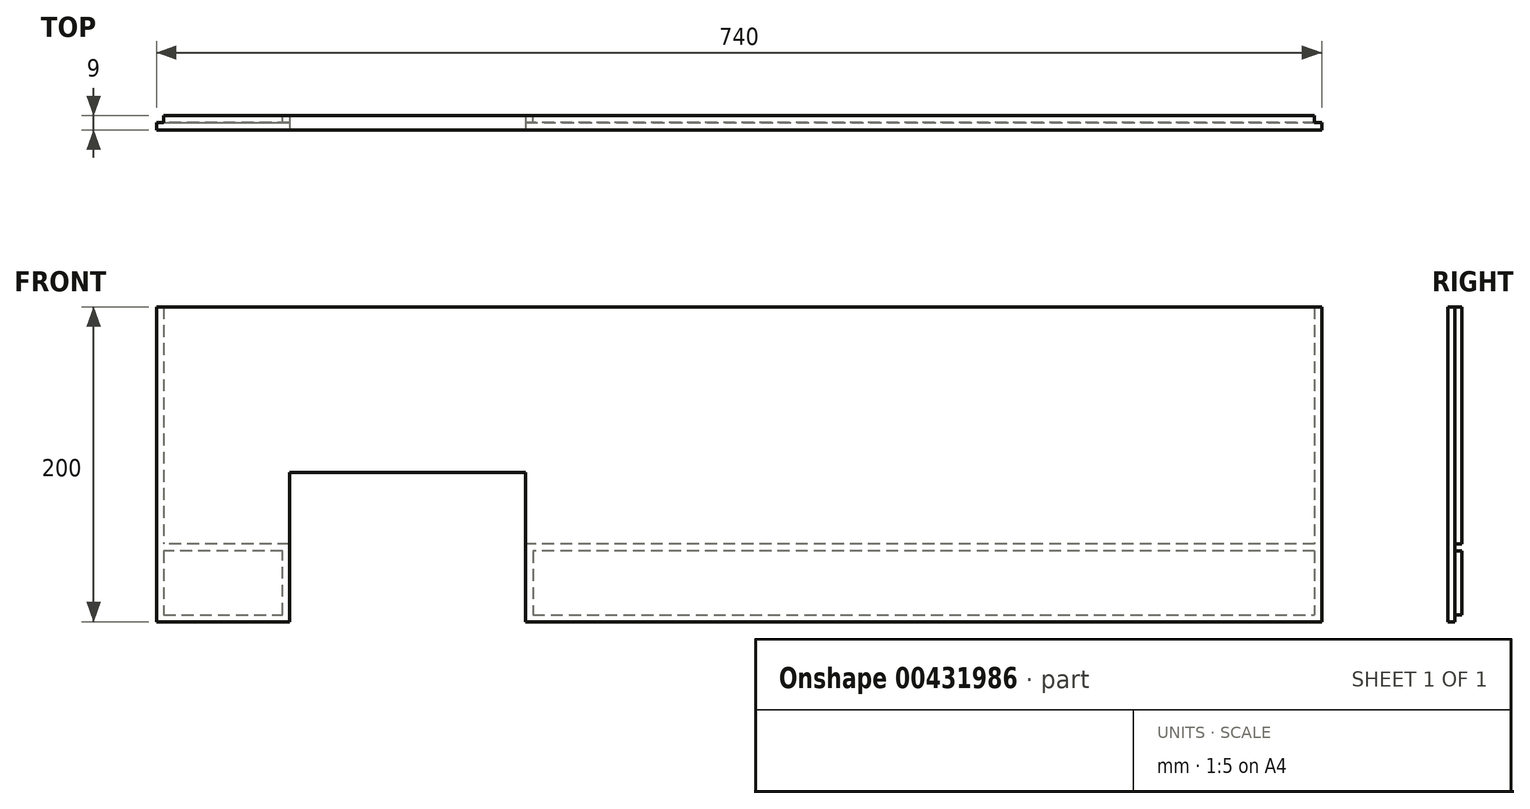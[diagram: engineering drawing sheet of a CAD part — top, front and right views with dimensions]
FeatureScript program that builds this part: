
annotation { "Feature Type Name" : "Feature", "Feature Type Description" : "" }
export const myFeature = defineFeature(function(context is Context, id is Id, definition is map)
    precondition{}
    {
        {
            var Q0;
            Q0=qCreatedBy(makeId("Front.planeOp"),FACE);
            var sketch = newSketch(context, id + "F0", { "sketchPlane" : qUnion([Q0])});
            skLineSegment(sketch, "E0.bottom", {"start": v(-370, 100) * mm, "end": v(370, 100) * mm});
            skLineSegment(sketch, "E0.top", {"start": v(-370, -100) * mm, "end": v(370, -100) * mm});
            skLineSegment(sketch, "E0.left", {"start": v(-370, 100) * mm, "end": v(-370, -100) * mm});
            skLineSegment(sketch, "E0.right", {"start": v(370, 100) * mm, "end": v(370, -100) * mm});
            skPoint(sketch, "E0.middle", {"position": v(0, 0) * mm});
            skSolve(sketch);
        }
        {
            var Q0;
            Q0=makeQuery(id+"F0.imprint","IMPRINT",FACE,{"disambiguationData":[TD([[makeQuery(id+"F0.imprint","IMPRINT",EDGE,{"derivedFrom":sQuery(id+"F0.wireOp",EDGE,"E0.bottom")}),-1.0]])]});
            extrude(context, id + "F1", {"entities" : qUnion([Q0]), "depth" : 9 * mm, "offsetDistance" : 25 * mm});
        }
        {
            var Q0;
            Q0=makeQuery(id+"F1.opExtrude","SWEPT_FACE",FACE,{"disambiguationData":[OSD([sQuery(id+"F0.wireOp",EDGE,"E0.right")])]});
            var sketch = newSketch(context, id + "F2", { "sketchPlane" : qUnion([Q0])});
            skLineSegment(sketch, "E1.bottom", {"start": v(0, 100) * mm, "end": v(-4.5, 100) * mm});
            skLineSegment(sketch, "E1.top", {"start": v(0, -100) * mm, "end": v(-4.5, -100) * mm});
            skLineSegment(sketch, "E1.left", {"start": v(0, 100) * mm, "end": v(0, -100) * mm});
            skLineSegment(sketch, "E1.right", {"start": v(-4.5, 100) * mm, "end": v(-4.5, -100) * mm});
            skSolve(sketch);
        }
        {
            var Q0;
            Q0=qSketchRegion(id+"F2",true);
            extrude(context, id + "F3", {"entities" : qUnion([Q0]), "operationType" : NewBodyOperationType.REMOVE, "oppositeDirection" : true, "depth" : 4.5 * mm, "offsetDistance" : 25 * mm});
        }
        {
            var Q0;
            Q0=makeQuery(id+"F1.opExtrude","SWEPT_FACE",FACE,{"disambiguationData":[OSD([sQuery(id+"F0.wireOp",EDGE,"E0.left")])]});
            var sketch = newSketch(context, id + "F4", { "sketchPlane" : qUnion([Q0])});
            skLineSegment(sketch, "E2.bottom", {"start": v(0, 100) * mm, "end": v(4.5, 100) * mm});
            skLineSegment(sketch, "E2.top", {"start": v(0, -100) * mm, "end": v(4.5, -100) * mm});
            skLineSegment(sketch, "E2.left", {"start": v(0, 100) * mm, "end": v(0, -100) * mm});
            skLineSegment(sketch, "E2.right", {"start": v(4.5, 100) * mm, "end": v(4.5, -100) * mm});
            skSolve(sketch);
        }
        {
            var Q0;
            Q0=qSketchRegion(id+"F4",true);
            extrude(context, id + "F5", {"entities" : qUnion([Q0]), "operationType" : NewBodyOperationType.REMOVE, "oppositeDirection" : true, "depth" : 4.5 * mm, "offsetDistance" : 25 * mm});
        }
        {
            var Q0;
            Q0=makeQuery(id+"F1.opExtrude","CAP_FACE",FACE,{"disambiguationData":[OSD([sQuery(id+"F0.wireOp",EDGE,"E0.bottom"),sQuery(id+"F0.wireOp",EDGE,"E0.top"),sQuery(id+"F0.wireOp",EDGE,"E0.left"),sQuery(id+"F0.wireOp",EDGE,"E0.right")])],"isStart":true});
            var sketch = newSketch(context, id + "F6", { "sketchPlane" : qUnion([Q0])});
            skLineSegment(sketch, "E3.bottom", {"start": v(-365.5, -50.5) * mm, "end": v(365.5, -50.5) * mm});
            skLineSegment(sketch, "E3.top", {"start": v(-365.5, -55) * mm, "end": v(365.5, -55) * mm});
            skLineSegment(sketch, "E3.left", {"start": v(-365.5, -50.5) * mm, "end": v(-365.5, -55) * mm});
            skLineSegment(sketch, "E3.right", {"start": v(365.5, -50.5) * mm, "end": v(365.5, -55) * mm});
            skSolve(sketch);
        }
        {
            var Q0;
            Q0=qSketchRegion(id+"F6",true);
            extrude(context, id + "F7", {"entities" : qUnion([Q0]), "operationType" : NewBodyOperationType.REMOVE, "oppositeDirection" : true, "depth" : 4.5 * mm, "offsetDistance" : 25 * mm});
        }
        {
            var Q0;
            {var subQ0=sQuery(id+"F0.wireOp",EDGE,"E0.top");Q0=makeQuery(id+"F7.boolean.opBoolean","SPLIT",FACE,{"disambiguationData":[TD([makeQuery(id+"F1.opExtrude","SWEPT_FACE",FACE,{"disambiguationData":[OSD([subQ0])]})])],"derivedFrom":makeQuery(id+"F1.opExtrude","CAP_FACE",FACE,{"disambiguationData":[OSD([sQuery(id+"F0.wireOp",EDGE,"E0.bottom"),subQ0,sQuery(id+"F0.wireOp",EDGE,"E0.left"),sQuery(id+"F0.wireOp",EDGE,"E0.right")])],"isStart":true})});}
            var sketch = newSketch(context, id + "F8", { "sketchPlane" : qUnion([Q0])});
            skLineSegment(sketch, "E4.bottom", {"start": v(365.5, -100) * mm, "end": v(-365.5, -100) * mm});
            skLineSegment(sketch, "E4.top", {"start": v(365.5, -95.5) * mm, "end": v(-365.5, -95.5) * mm});
            skLineSegment(sketch, "E4.left", {"start": v(365.5, -100) * mm, "end": v(365.5, -95.5) * mm});
            skLineSegment(sketch, "E4.right", {"start": v(-365.5, -100) * mm, "end": v(-365.5, -95.5) * mm});
            skSolve(sketch);
        }
        {
            var Q0;
            Q0=qSketchRegion(id+"F8",true);
            extrude(context, id + "F9", {"entities" : qUnion([Q0]), "operationType" : NewBodyOperationType.REMOVE, "oppositeDirection" : true, "depth" : 4.5 * mm, "offsetDistance" : 25 * mm});
        }
        {
            var Q0;
            Q0=makeQuery(id+"F1.opExtrude","CAP_FACE",FACE,{"disambiguationData":[OSD([sQuery(id+"F0.wireOp",EDGE,"E0.bottom"),sQuery(id+"F0.wireOp",EDGE,"E0.top"),sQuery(id+"F0.wireOp",EDGE,"E0.left"),sQuery(id+"F0.wireOp",EDGE,"E0.right")])],"isStart":false});
            var sketch = newSketch(context, id + "F10", { "sketchPlane" : qUnion([Q0])});
            skLineSegment(sketch, "E5.bottom", {"start": v(-285.5, -100) * mm, "end": v(-135.5, -100) * mm});
            skLineSegment(sketch, "E5.top", {"start": v(-285.5, -5) * mm, "end": v(-135.5, -5) * mm});
            skLineSegment(sketch, "E5.left", {"start": v(-285.5, -100) * mm, "end": v(-285.5, -5) * mm});
            skLineSegment(sketch, "E5.right", {"start": v(-135.5, -100) * mm, "end": v(-135.5, -5) * mm});
            skSolve(sketch);
        }
        {
            var Q0;
            Q0=qSketchRegion(id+"F10",true);
            extrude(context, id + "F11", {"entities" : qUnion([Q0]), "operationType" : NewBodyOperationType.REMOVE, "oppositeDirection" : true, "depth" : 25 * mm});
        }
        {
            var Q0;
            {var subQ2=sQuery(id+"F0.wireOp",EDGE,"E0.top");Q0=makeQuery(id+"F11.boolean.opBoolean","SPLIT",FACE,{"disambiguationData":[TD([makeQuery(id+"F11.opExtrude","SWEPT_FACE",FACE,{"disambiguationData":[OSD([sQuery(id+"F10.wireOp",EDGE,"E5.right")])]})])],"derivedFrom":makeQuery(id+"F7.boolean.opBoolean","SPLIT",FACE,{"disambiguationData":[TD([makeQuery(id+"F1.opExtrude","SWEPT_FACE",FACE,{"disambiguationData":[OSD([subQ2])]})])],"derivedFrom":makeQuery(id+"F1.opExtrude","CAP_FACE",FACE,{"disambiguationData":[OSD([sQuery(id+"F0.wireOp",EDGE,"E0.bottom"),subQ2,sQuery(id+"F0.wireOp",EDGE,"E0.left"),sQuery(id+"F0.wireOp",EDGE,"E0.right")])],"isStart":true})})});}
            var sketch = newSketch(context, id + "F12", { "sketchPlane" : qUnion([Q0])});
            skLineSegment(sketch, "E6.bottom", {"start": v(135.5, -55) * mm, "end": v(131, -55) * mm});
            skLineSegment(sketch, "E6.top", {"start": v(135.5, -95.5) * mm, "end": v(131, -95.5) * mm});
            skLineSegment(sketch, "E6.left", {"start": v(135.5, -55) * mm, "end": v(135.5, -95.5) * mm});
            skLineSegment(sketch, "E6.right", {"start": v(131, -55) * mm, "end": v(131, -95.5) * mm});
            skSolve(sketch);
        }
        {
            var Q0;
            Q0=qSketchRegion(id+"F12",true);
            extrude(context, id + "F13", {"entities" : qUnion([Q0]), "operationType" : NewBodyOperationType.REMOVE, "oppositeDirection" : true, "depth" : 4.5 * mm, "offsetDistance" : 25 * mm});
        }
        {
            var Q0;
            {var subQ2=sQuery(id+"F0.wireOp",EDGE,"E0.top");Q0=makeQuery(id+"F11.boolean.opBoolean","SPLIT",FACE,{"disambiguationData":[TD([makeQuery(id+"F11.opExtrude","SWEPT_FACE",FACE,{"disambiguationData":[OSD([sQuery(id+"F10.wireOp",EDGE,"E5.left")])]})])],"derivedFrom":makeQuery(id+"F7.boolean.opBoolean","SPLIT",FACE,{"disambiguationData":[TD([makeQuery(id+"F1.opExtrude","SWEPT_FACE",FACE,{"disambiguationData":[OSD([subQ2])]})])],"derivedFrom":makeQuery(id+"F1.opExtrude","CAP_FACE",FACE,{"disambiguationData":[OSD([sQuery(id+"F0.wireOp",EDGE,"E0.bottom"),subQ2,sQuery(id+"F0.wireOp",EDGE,"E0.left"),sQuery(id+"F0.wireOp",EDGE,"E0.right")])],"isStart":true})})});}
            var sketch = newSketch(context, id + "F14", { "sketchPlane" : qUnion([Q0])});
            skLineSegment(sketch, "E7.bottom", {"start": v(285.5, -95.5) * mm, "end": v(290, -95.5) * mm});
            skLineSegment(sketch, "E7.top", {"start": v(285.5, -55) * mm, "end": v(290, -55) * mm});
            skLineSegment(sketch, "E7.left", {"start": v(285.5, -95.5) * mm, "end": v(285.5, -55) * mm});
            skLineSegment(sketch, "E7.right", {"start": v(290, -95.5) * mm, "end": v(290, -55) * mm});
            skSolve(sketch);
        }
        {
            var Q0;
            Q0=qSketchRegion(id+"F14",true);
            extrude(context, id + "F15", {"entities" : qUnion([Q0]), "operationType" : NewBodyOperationType.REMOVE, "oppositeDirection" : true, "depth" : 4.5 * mm, "offsetDistance" : 25 * mm});
        }
    });
